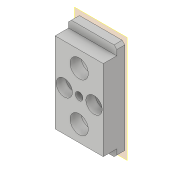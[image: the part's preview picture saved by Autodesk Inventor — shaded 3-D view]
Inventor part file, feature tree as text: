
AUTODESK INVENTOR PART (.ipt)
format: ipt  version: 2019.4 (Build 234330000, 330)  size: 232,448 bytes
history: native  units: mm
features: sketch x8, extrude x7, projected_geometry x5, plane x4, reference x4, other x4, hole x1
ambient origin geometry x8: Origin, YZ Plane, XZ Plane, XY Plane, X Axis, Y Axis, Z Axis, Center Point
bodies: Solid1 (feature_tree)
feature tree (33):
  plane  "Work Plane1"
  sketch  "Sketch1"  dims[d0=10.0mm d1=0.0mm d2=5.5mm]
  plane  "Work Plane2"
  plane  "Work Plane3"
  extrude  "Extrusion1"  Depth=10.0mm
  hole  "Hole1"  [1 undecoded]
  extrude  "Extrusion2"  Depth=10.0mm TaperAngle=0.0deg
  extrude  "Extrusion3"  Depth=7.8mm
  extrude  "Extrusion4"  Depth=1.5mm
  plane  "Work Plane4"
  extrude  "Extrusion5"  Depth=3.0mm
  extrude  "Extrusion6"  Depth=4.0mm TaperAngle=0.0deg
  extrude  "Extrusion7"  Depth=3.0mm
  reference  "Reference1"
  sketch  "Sketch2"  dims[d3=5.5mm]
  projected_geometry  "Projected Loop1"
  sketch  "Sketch3"  dims[d4=2.9mm d5=6.0mm d6=6.0mm d7=3.5mm d8=90.0deg d9=8.0mm d10=20.594885mm d11=6.75mm]
  reference  "Reference2"
  reference  "Reference3"
  sketch  "Sketch4"  dims[d12=6.75mm d13=10.0mm d14=0.0mm]
  sketch  "Sketch5"  dims[d15=7.8mm d16=7.8mm]
  reference  "Reference4"
  projected_geometry  "Projected Loop2"
  sketch  "Sketch6"  dims[d17=4.0mm d18=0.0mm d19=1.5mm]
  projected_geometry  "Projected Loop3"
  sketch  "Sketch7"  dims[d20=3.0mm d21=0.0mm d22=3.0mm]
  projected_geometry  "Projected Loop4"
  sketch  "Sketch8"  dims[d23=3.0mm d24=4.0mm d25=0.0mm d26=3.0mm d27=3.0mm d28=10.0mm d29=0.0mm d30=10.0mm d31=0.0mm]
  projected_geometry  "Projected Loop5"
  other  "Assembly_Omniscope_v1.iam"
  other  "01_Camera_Module_left_v0:1"
  other  "00_OV_lens:2"
  other  "00_OV_lens:1"
note: 1 required parameter value undecoded (feature->parameter linkage not recoverable at this tier; creation-order binding heuristic only, values carry confidence <= 0.55)
